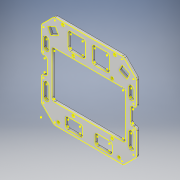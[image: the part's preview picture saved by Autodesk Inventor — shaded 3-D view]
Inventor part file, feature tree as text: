
AUTODESK INVENTOR PART (.ipt)
format: ipt  version: 2019 (Build 230136000, 136)  size: 434,688 bytes
history: native  units: mm
features: sketch x2, hole x2, fillet x2, extrude x1, chamfer x1, projected_geometry x1
ambient origin geometry x8: Origin, YZ Plane, XZ Plane, XY Plane, X Axis, Y Axis, Z Axis, Center Point
bodies: Solid1 (feature_tree)
feature tree (9):
  sketch  "Sketch1"  dims[d0=60.0mm d1=100.0mm]
  extrude  "Extrusion1"  Depth=100.0mm
  hole  "Hole1"  [1 undecoded]
  fillet  "Fillet1"  Radius=108.0mm
  chamfer  "Chamfer1"  Distance=35.0mm
  fillet  "Fillet2"  Radius=5.0mm
  sketch  "Sketch5"  dims[d2=70.0mm d3=110.0mm d4=108.0mm d6=35.0mm d7=5.0mm d8=85.0mm d9=54.0mm d10=25.0mm d11=45.0mm d12=60.0mm d13=12.5mm d14=23.0mm d15=55.0mm d16=70.0mm d17=5.0mm d18=5.0mm d23=28.0mm d24=20.0mm d29=7.0mm d30=20.0mm d35=12.5mm d36=12.5mm d38=20.0mm d39=20.0mm d40=25.0mm d41=45.0mm d42=28.0mm d43=20.0mm d44=20.0mm d46=31.0mm d47=6.0mm d48=15.0mm d49=6.0mm d50=15.0mm d51=3.0mm d52=3.0mm d53=31.0mm d54=20.0mm d55=13.0mm d56=20.0mm d57=13.0mm d58=28.0mm d59=28.0mm d60=7.0mm d62=7.0mm d63=20.0mm d64=6.0mm d65=20.0mm d66=6.0mm d67=20.0mm d68=3.0mm d69=3.0mm d70=5.0mm d71=5.0mm d72=5.0mm d73=7.0mm d74=19.0mm d75=5.0mm d137=20.0mm d138=16.0mm d139=20.0mm d140=16.0mm d141=60.0mm d142=100.0mm d143=70.0mm d144=110.0mm d145=108.0mm d146=35.0mm d147=5.0mm d148=85.0mm d149=54.0mm d150=45.0mm d151=60.0mm d152=23.0mm d153=55.0mm d154=70.0mm d155=5.0mm d156=5.0mm d157=28.0mm d158=20.0mm d159=7.0mm d160=20.0mm d161=12.5mm d162=12.5mm d163=20.0mm d164=20.0mm d165=25.0mm d166=45.0mm d167=28.0mm d168=20.0mm d169=20.0mm d170=31.0mm d171=6.0mm d172=20.0mm d173=6.0mm d174=20.0mm d175=3.0mm d176=3.0mm d177=31.0mm d178=20.0mm d179=13.0mm d180=20.0mm d181=13.0mm d182=28.0mm d183=28.0mm d184=7.0mm d185=7.0mm d186=20.0mm d187=6.0mm d188=20.0mm d189=6.0mm d190=20.0mm d191=3.0mm d192=3.0mm d193=5.0mm d194=5.0mm d195=5.0mm d196=7.0mm d197=19.0mm d198=5.0mm d199=20.0mm d200=16.0mm d201=20.0mm d202=16.0mm d203=10.0mm d204=8.0mm d205=3.0mm d206=0.0mm d207=3.3mm d208=6.0mm d209=4.0mm d210=2.0mm d211=90.0deg d212=8.0mm d213=20.594885mm d214=3.0mm d215=15.0mm d216=2.0mm d217=45.0deg d218=3.0mm]
  hole  "Holes"  [1 undecoded]
  projected_geometry  "Projected Loop1"
note: 2 required parameter values undecoded (feature->parameter linkage not recoverable at this tier; creation-order binding heuristic only, values carry confidence <= 0.55)
